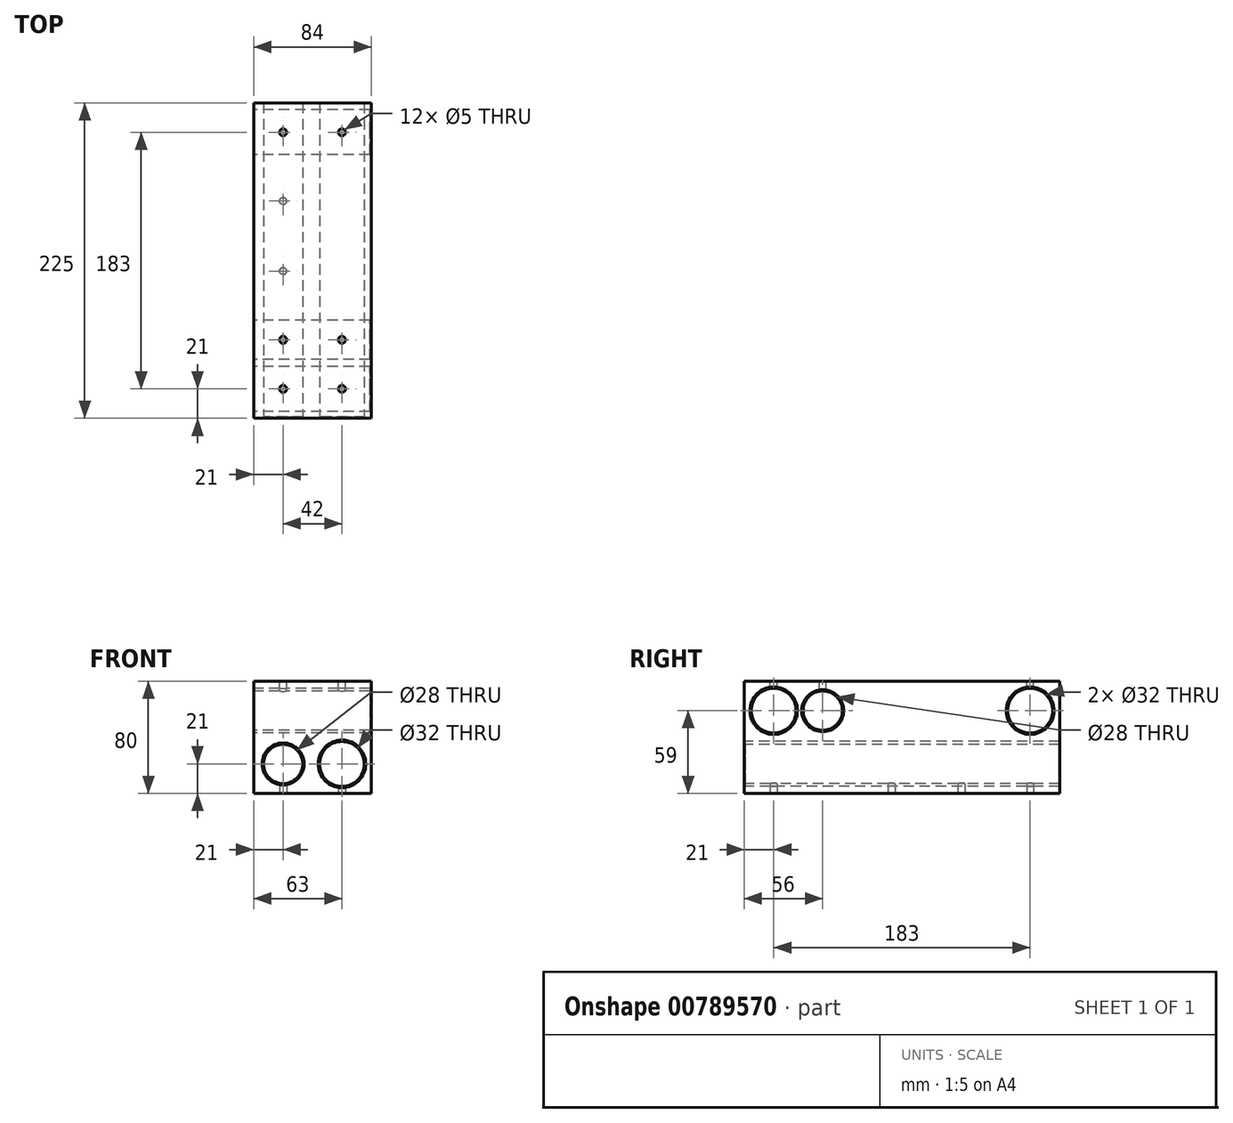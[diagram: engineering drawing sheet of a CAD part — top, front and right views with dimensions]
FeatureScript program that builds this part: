
annotation { "Feature Type Name" : "Feature", "Feature Type Description" : "" }
export const myFeature = defineFeature(function(context is Context, id is Id, definition is map)
    precondition{}
    {
        {
            var Q0;
            Q0=qCreatedBy(makeId("Front.planeOp"),FACE);
            var sketch = newSketch(context, id + "F0", { "sketchPlane" : qUnion([Q0])});
            skLineSegment(sketch, "E0.bottom", {"start": v(42, 40) * mm, "end": v(-42, 40) * mm});
            skLineSegment(sketch, "E0.top", {"start": v(42, -40) * mm, "end": v(-42, -40) * mm});
            skLineSegment(sketch, "E0.left", {"start": v(42, 40) * mm, "end": v(42, -40) * mm});
            skLineSegment(sketch, "E0.right", {"start": v(-42, 40) * mm, "end": v(-42, -40) * mm});
            skPoint(sketch, "E0.middle", {"position": v(0, 0) * mm});
            skPoint(sketch, "E1", {"position": v(-21, -19) * mm});
            skPoint(sketch, "E2", {"position": v(21, -19) * mm});
            skCircle(sketch, "E3", {"center": v(-21, -19) * mm, "radius": 14 * mm});
            skCircle(sketch, "E4", {"center": v(21, -19) * mm, "radius": 16 * mm});
            skSolve(sketch);
        }
        {
            var Q0;
            Q0 = qSketchRegion(id + "F0", true);
            extrude(context, id + "F1", {"entities" : qUnion([Q0]), "oppositeDirection" : true, "depth" : 225 * mm, "offsetDistance" : 25 * mm});
        }
        {
            var Q0;
            Q0=makeQuery(id+"F1.opExtrude","SWEPT_FACE",FACE,{"disambiguationData":[OSD([sQuery(id+"F0.wireOp",EDGE,"E0.right")])]});
            var sketch = newSketch(context, id + "F2", { "sketchPlane" : qUnion([Q0])});
            skPoint(sketch, "E5", {"position": v(-56, 19) * mm});
            skPoint(sketch, "E6", {"position": v(-21, 19) * mm});
            skPoint(sketch, "E7", {"position": v(-204, 19) * mm});
            skCircle(sketch, "E8", {"center": v(-204, 19) * mm, "radius": 16 * mm});
            skCircle(sketch, "E9", {"center": v(-56, 19) * mm, "radius": 14 * mm});
            skCircle(sketch, "E10", {"center": v(-21, 19) * mm, "radius": 16 * mm});
            skSolve(sketch);
        }
        {
            var Q0;
            Q0 = qSketchRegion(id + "F2", true);
            extrude(context, id + "F3", {"entities" : qUnion([Q0]), "operationType" : NewBodyOperationType.REMOVE, "oppositeDirection" : true, "depth" : 100 * mm, "offsetDistance" : 25 * mm});
        }
        {
            var Q0;
            Q0=makeQuery(id+"F3.boolean.opBoolean","COPY",EDGE,{"derivedFrom":makeQuery(id+"F3.opExtrude","CAP_EDGE",EDGE,{"disambiguationData":[OSD([sQuery(id+"F2.wireOp",EDGE,"E8")])],"isStart":true})});
            var Q1;
            Q1=makeQuery(id+"F3.boolean.opBoolean","COPY",EDGE,{"derivedFrom":makeQuery(id+"F3.opExtrude","CAP_EDGE",EDGE,{"disambiguationData":[OSD([sQuery(id+"F2.wireOp",EDGE,"E9")])],"isStart":true})});
            var Q2;
            Q2=makeQuery(id+"F3.boolean.opBoolean","COPY",EDGE,{"derivedFrom":makeQuery(id+"F3.opExtrude","CAP_EDGE",EDGE,{"disambiguationData":[OSD([sQuery(id+"F2.wireOp",EDGE,"E10")])],"isStart":true})});
            var Q3;
            Q3=makeQuery(id+"F1.opExtrude","CAP_EDGE",EDGE,{"disambiguationData":[OSD([sQuery(id+"F0.wireOp",EDGE,"E3")])],"isStart":true});
            var Q4;
            Q4=makeQuery(id+"F1.opExtrude","CAP_EDGE",EDGE,{"disambiguationData":[OSD([sQuery(id+"F0.wireOp",EDGE,"E4")])],"isStart":true});
            var Q5;
            Q5=makeQuery(id+"F3.boolean.opBoolean","INTERSECT",EDGE,{"derivedFrom":[makeQuery(id+"F1.opExtrude","SWEPT_FACE",FACE,{"disambiguationData":[OSD([sQuery(id+"F0.wireOp",EDGE,"E0.left")])]}),makeQuery(id+"F3.opExtrude","SWEPT_FACE",FACE,{"disambiguationData":[OSD([sQuery(id+"F2.wireOp",EDGE,"E10")])]})]});
            var Q6;
            Q6=makeQuery(id+"F3.boolean.opBoolean","INTERSECT",EDGE,{"derivedFrom":[makeQuery(id+"F1.opExtrude","SWEPT_FACE",FACE,{"disambiguationData":[OSD([sQuery(id+"F0.wireOp",EDGE,"E0.left")])]}),makeQuery(id+"F3.opExtrude","SWEPT_FACE",FACE,{"disambiguationData":[OSD([sQuery(id+"F2.wireOp",EDGE,"E9")])]})]});
            var Q7;
            Q7=makeQuery(id+"F3.boolean.opBoolean","INTERSECT",EDGE,{"derivedFrom":[makeQuery(id+"F1.opExtrude","SWEPT_FACE",FACE,{"disambiguationData":[OSD([sQuery(id+"F0.wireOp",EDGE,"E0.left")])]}),makeQuery(id+"F3.opExtrude","SWEPT_FACE",FACE,{"disambiguationData":[OSD([sQuery(id+"F2.wireOp",EDGE,"E8")])]})]});
            chamfer(context, id + "F4", {"entities" : qUnion([Q0, Q1, Q2, Q3, Q4, Q5, Q6, Q7]), "width" : 1 * mm, "tangentPropagation" : true});
        }
        {
            var Q0;
            Q0=makeQuery(id+"F1.opExtrude","SWEPT_FACE",FACE,{"disambiguationData":[OSD([sQuery(id+"F0.wireOp",EDGE,"E0.bottom")])]});
            var sketch = newSketch(context, id + "F5", { "sketchPlane" : qUnion([Q0])});
            skPoint(sketch, "E11", {"position": v(21, 204) * mm});
            skPoint(sketch, "E12", {"position": v(-21, 204) * mm});
            skPoint(sketch, "E13", {"position": v(-21, 56) * mm});
            skPoint(sketch, "E14", {"position": v(-21, 21) * mm});
            skPoint(sketch, "E15", {"position": v(21, 21) * mm});
            skPoint(sketch, "E16", {"position": v(21, 56) * mm});
            skCircle(sketch, "E17", {"center": v(21, 204) * mm, "radius": 2.5 * mm});
            skCircle(sketch, "E18", {"center": v(-21, 204) * mm, "radius": 2.5 * mm});
            skCircle(sketch, "E19", {"center": v(21, 56) * mm, "radius": 2.5 * mm});
            skCircle(sketch, "E20", {"center": v(-21, 56) * mm, "radius": 2.5 * mm});
            skCircle(sketch, "E21", {"center": v(-21, 21) * mm, "radius": 2.5 * mm});
            skCircle(sketch, "E22", {"center": v(21, 21) * mm, "radius": 2.5 * mm});
            skSolve(sketch);
        }
        {
            var Q0;
            Q0=makeQuery(id+"F5.imprint","IMPRINT",FACE,{"disambiguationData":[TD([[makeQuery(id+"F5.imprint","IMPRINT",EDGE,{"derivedFrom":sQuery(id+"F5.wireOp",EDGE,"E17")}),1.0]])]});
            var Q1;
            Q1=makeQuery(id+"F5.imprint","IMPRINT",FACE,{"disambiguationData":[TD([[makeQuery(id+"F5.imprint","IMPRINT",EDGE,{"derivedFrom":sQuery(id+"F5.wireOp",EDGE,"E19")}),1.0]])]});
            var Q2;
            Q2=makeQuery(id+"F5.imprint","IMPRINT",FACE,{"disambiguationData":[TD([[makeQuery(id+"F5.imprint","IMPRINT",EDGE,{"derivedFrom":sQuery(id+"F5.wireOp",EDGE,"E22")}),1.0]])]});
            var Q3;
            Q3=makeQuery(id+"F5.imprint","IMPRINT",FACE,{"disambiguationData":[TD([[makeQuery(id+"F5.imprint","IMPRINT",EDGE,{"derivedFrom":sQuery(id+"F5.wireOp",EDGE,"E21")}),1.0]])]});
            var Q4;
            Q4=makeQuery(id+"F5.imprint","IMPRINT",FACE,{"disambiguationData":[TD([[makeQuery(id+"F5.imprint","IMPRINT",EDGE,{"derivedFrom":sQuery(id+"F5.wireOp",EDGE,"E20")}),1.0]])]});
            var Q5;
            Q5=makeQuery(id+"F5.imprint","IMPRINT",FACE,{"disambiguationData":[TD([[makeQuery(id+"F5.imprint","IMPRINT",EDGE,{"derivedFrom":sQuery(id+"F5.wireOp",EDGE,"E18")}),1.0]])]});
            extrude(context, id + "F6", {"entities" : qUnion([Q0, Q1, Q2, Q3, Q4, Q5]), "operationType" : NewBodyOperationType.REMOVE, "oppositeDirection" : true, "depth" : 25 * mm, "offsetDistance" : 25 * mm});
        }
        {
            var Q0;
            Q0=makeQuery(id+"F1.opExtrude","SWEPT_FACE",FACE,{"disambiguationData":[OSD([sQuery(id+"F0.wireOp",EDGE,"E0.top")])]});
            var sketch = newSketch(context, id + "F7", { "sketchPlane" : qUnion([Q0])});
            skPoint(sketch, "E23", {"position": v(-21, -21) * mm});
            skPoint(sketch, "E24", {"position": v(21, -21) * mm});
            skPoint(sketch, "E25", {"position": v(-21, -105) * mm});
            skPoint(sketch, "E26", {"position": v(-21, -155) * mm});
            skPoint(sketch, "E27", {"position": v(-21, -204) * mm});
            skPoint(sketch, "E28", {"position": v(21, -204) * mm});
            skCircle(sketch, "E29", {"center": v(-21, -204) * mm, "radius": 2.5 * mm});
            skCircle(sketch, "E30", {"center": v(21, -204) * mm, "radius": 2.5 * mm});
            skCircle(sketch, "E31", {"center": v(-21, -155) * mm, "radius": 2.5 * mm});
            skCircle(sketch, "E32", {"center": v(-21, -105) * mm, "radius": 2.5 * mm});
            skCircle(sketch, "E33", {"center": v(-21, -21) * mm, "radius": 2.5 * mm});
            skCircle(sketch, "E34", {"center": v(21, -21) * mm, "radius": 2.5 * mm});
            skLineSegment(sketch, "E35", {"start": v(-21, -105) * mm, "end": v(-21, -155) * mm});
            skPoint(sketch, "E36", {"position": v(-21, -130) * mm});
            skSolve(sketch);
        }
        {
            var Q0;
            Q0=makeQuery(id+"F7.imprint","IMPRINT",FACE,{"disambiguationData":[TD([[makeQuery(id+"F7.imprint","IMPRINT",EDGE,{"derivedFrom":sQuery(id+"F7.wireOp",EDGE,"HRyMPZyD-e41J-6McJ-Vndr-79CBD1wgSbvk")}),1.0]])]});
            var Q1;
            Q1=makeQuery(id+"F7.imprint","IMPRINT",FACE,{"disambiguationData":[TD([[makeQuery(id+"F7.imprint","IMPRINT",EDGE,{"derivedFrom":sQuery(id+"F7.wireOp",EDGE,"E33")}),1.0]])]});
            var Q2;
            Q2=makeQuery(id+"F7.imprint","IMPRINT",FACE,{"disambiguationData":[TD([[makeQuery(id+"F7.imprint","IMPRINT",EDGE,{"derivedFrom":sQuery(id+"F7.wireOp",EDGE,"E34")}),1.0]])]});
            var Q3;
            Q3=makeQuery(id+"F7.imprint","IMPRINT",FACE,{"disambiguationData":[TD([[makeQuery(id+"F7.imprint","IMPRINT",EDGE,{"derivedFrom":sQuery(id+"F7.wireOp",EDGE,"bvqbZPAr-1tDH-wyYk-Vviw-JCDYL4xZX3rK")}),1.0]])]});
            var Q4;
            Q4=makeQuery(id+"F7.imprint","IMPRINT",FACE,{"disambiguationData":[TD([[makeQuery(id+"F7.imprint","IMPRINT",EDGE,{"derivedFrom":sQuery(id+"F7.wireOp",EDGE,"E32")}),1.0]])]});
            var Q5;
            Q5=makeQuery(id+"F7.imprint","IMPRINT",FACE,{"disambiguationData":[TD([[makeQuery(id+"F7.imprint","IMPRINT",EDGE,{"derivedFrom":sQuery(id+"F7.wireOp",EDGE,"E31")}),1.0]])]});
            var Q6;
            Q6=makeQuery(id+"F7.imprint","IMPRINT",FACE,{"disambiguationData":[TD([[makeQuery(id+"F7.imprint","IMPRINT",EDGE,{"derivedFrom":sQuery(id+"F7.wireOp",EDGE,"E29")}),1.0]])]});
            var Q7;
            Q7=makeQuery(id+"F7.imprint","IMPRINT",FACE,{"disambiguationData":[TD([[makeQuery(id+"F7.imprint","IMPRINT",EDGE,{"derivedFrom":sQuery(id+"F7.wireOp",EDGE,"E30")}),1.0]])]});
            extrude(context, id + "F8", {"entities" : qUnion([Q0, Q1, Q2, Q3, Q4, Q5, Q6, Q7]), "operationType" : NewBodyOperationType.REMOVE, "oppositeDirection" : true, "depth" : 25 * mm, "offsetDistance" : 25 * mm});
        }
    });
